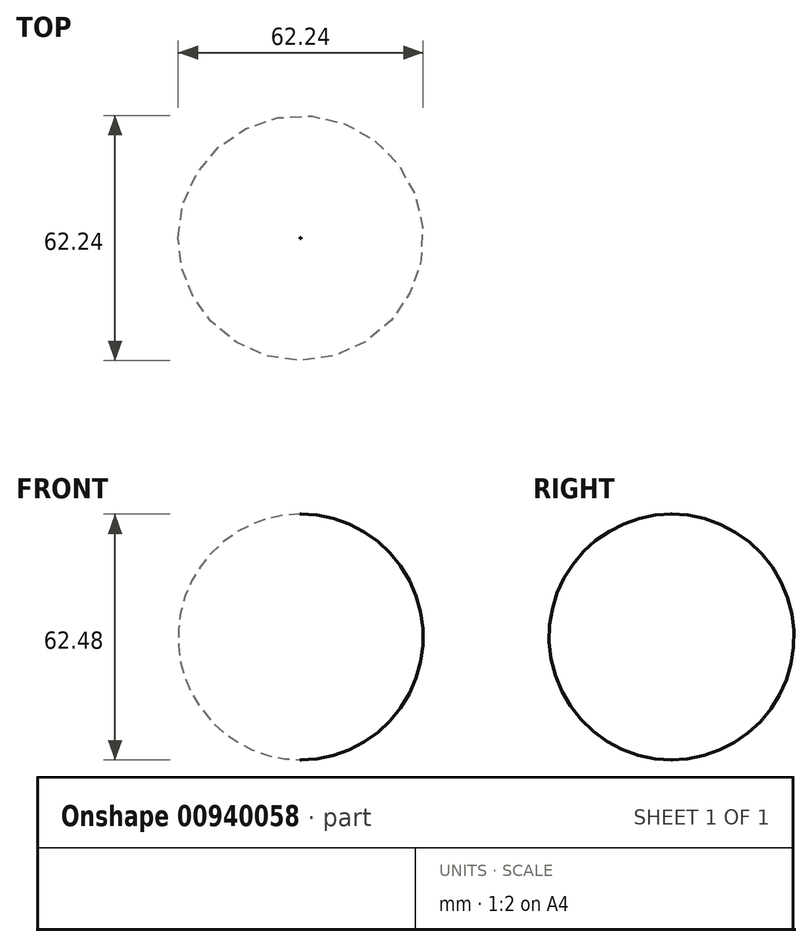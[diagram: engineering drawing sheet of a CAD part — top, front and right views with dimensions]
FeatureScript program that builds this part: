
annotation { "Feature Type Name" : "Feature", "Feature Type Description" : "" }
export const myFeature = defineFeature(function(context is Context, id is Id, definition is map)
    precondition{}
    {
        {
            var Q0;
            Q0=qCreatedBy(makeId("Top.planeOp"),FACE);
            var sketch = newSketch(context, id + "F0", { "sketchPlane" : qUnion([Q0])});
            skCircle(sketch, "E0", {"center": v(0, 0) * mm, "radius": 31.36 * mm});
            skSolve(sketch);
        }
        {
            var Q0;
            Q0=makeQuery(id+"F0.imprint","IMPRINT",FACE,{"disambiguationData":[TD([[makeQuery(id+"F0.imprint","IMPRINT",EDGE,{"derivedFrom":sQuery(id+"F0.wireOp",EDGE,"E0")}),1.0]])]});
            extrude(context, id + "F1", {"entities" : qUnion([Q0]), "endBound" : BoundingType.SYMMETRIC, "depth" : 62.48 * mm, "offsetDistance" : 25.4 * mm});
        }
        {
            var Q0;
            Q0=makeQuery(id+"F1.opExtrude","CAP_FACE",FACE,{"disambiguationData":[OSD([sQuery(id+"F0.wireOp",EDGE,"E0")])],"isStart":false});
            fillet(context, id + "F2", {"entities" : qUnion([Q0]), "radius" : 31.24 * mm, "tangentPropagation" : true, "allowEdgeOverflow" : false});
        }
        {
            var Q0;
            Q0=makeQuery(id+"F1.opExtrude","CAP_FACE",FACE,{"disambiguationData":[OSD([sQuery(id+"F0.wireOp",EDGE,"E0")])],"isStart":true});
            fillet(context, id + "F3", {"entities" : qUnion([Q0]), "radius" : 31.24 * mm, "tangentPropagation" : true, "allowEdgeOverflow" : false});
        }
    });
